# Revit family: 54963XXX_NEW
name_source: partatom
category: Furniture
units: mm (PartAtom-declared; Revit-internal decimal feet)

## family parameters
Always vertical = No
Cut with Voids When Loaded = No
OmniClass Number = 23.21.37.13.15
OmniClass Title = Mirrors
Room Calculation Point = No
Shared = No
Work Plane-Based = Yes

## types (2) — shared parameters
Connector Description = Power Supply
Default Elevation = 1219 mm
Description = Xarita Lite Q Mirror with lateral LED lights 800/30 wall switch
Manufacturer = Hansgrohe
Material 1 = Hansgrohe - Glass - Mirror
Material 2 = Hansgrohe - Glass - LED light
Model = 54963XXX
Product Guid = a0cd38ee-4bef-4038-afef-67aaeb9bd8f7
Product Page URL = https://www.hansgrohe.com
Product data url = https://bimobject.com
URL = https://www.hansgrohe.com
Version = 1
Voltage = 230 V

## per-type parameters (varying)
| type | Material |
| 670 Matte Black | Hansgrohe - Metal - 670 Matte Black |
| 700 Matte White | Hansgrohe - Metal - 700 Matte White |

## geometry (parser evidence)
native form markers: Sweep x3
no freeform markers — native parametric forms only
